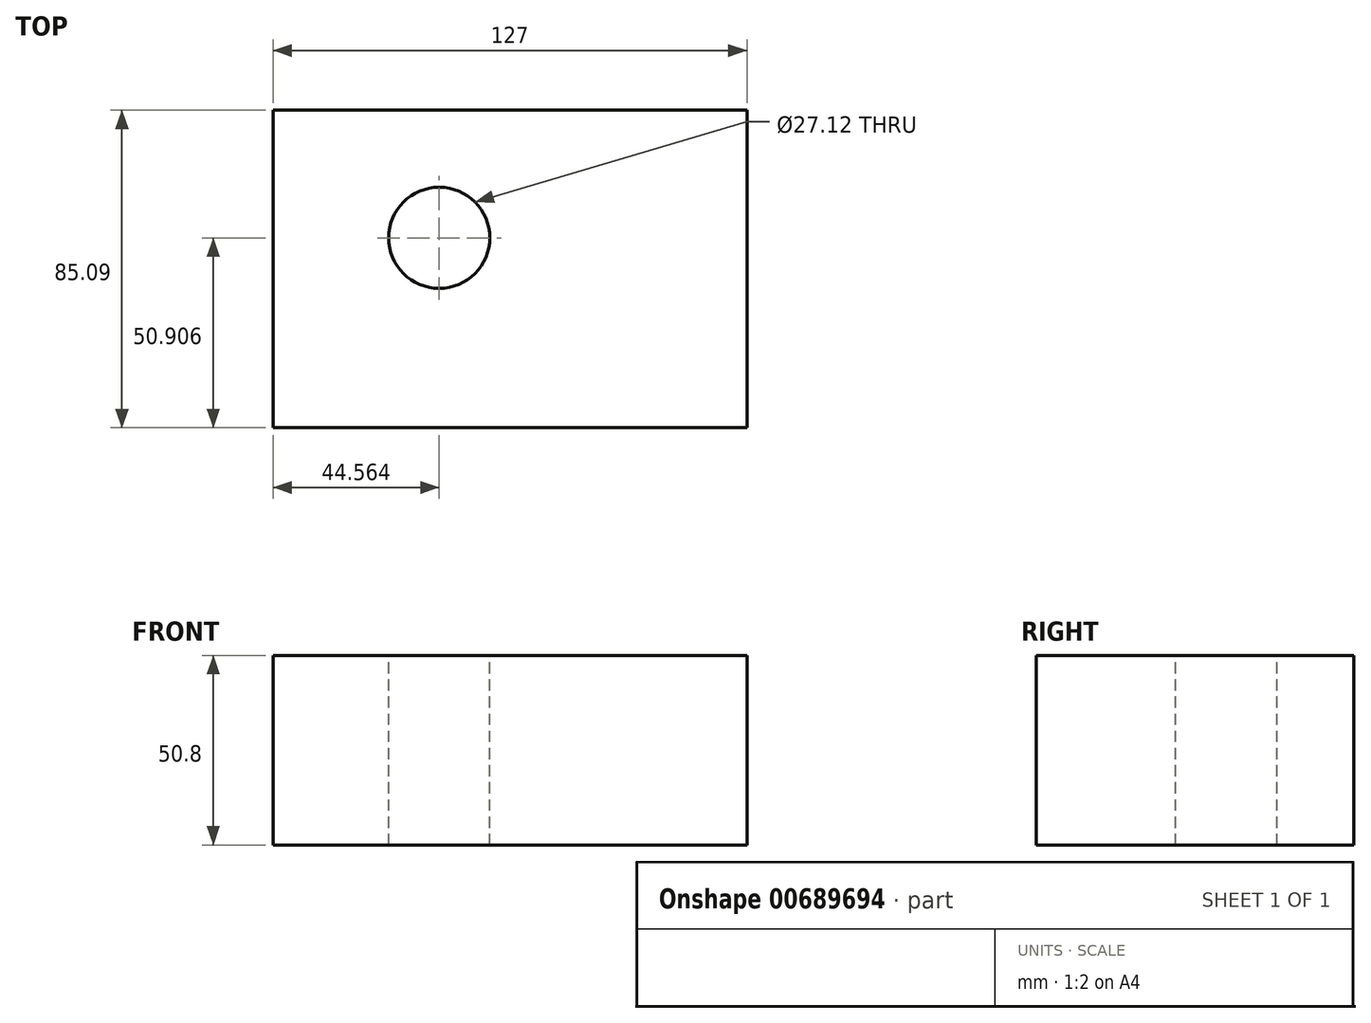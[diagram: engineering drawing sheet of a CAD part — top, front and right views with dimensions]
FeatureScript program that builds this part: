
annotation { "Feature Type Name" : "Feature", "Feature Type Description" : "" }
export const myFeature = defineFeature(function(context is Context, id is Id, definition is map)
    precondition{}
    {
        {
            var Q0;
            Q0=qCreatedBy(makeId("Front.planeOp"),FACE);
            var sketch = newSketch(context, id + "F0", { "sketchPlane" : qUnion([Q0])});
            skLineSegment(sketch, "E0.bottom", {"start": v(-99.64, 38.38) * mm, "end": v(27.36, 38.38) * mm});
            skLineSegment(sketch, "E0.top", {"start": v(-99.64, -12.42) * mm, "end": v(27.36, -12.42) * mm});
            skLineSegment(sketch, "E0.left", {"start": v(-99.64, 38.38) * mm, "end": v(-99.64, -12.42) * mm});
            skLineSegment(sketch, "E0.right", {"start": v(27.36, 38.38) * mm, "end": v(27.36, -12.42) * mm});
            skSolve(sketch);
        }
        {
            var Q0;
            Q0 = qSketchRegion(id + "F0", true);
            extrude(context, id + "F1", {"entities" : qUnion([Q0]), "depth" : 85.1 * mm, "offsetDistance" : 25.4 * mm});
        }
        {
            var Q0;
            Q0=makeQuery(id+"F1.opExtrude","SWEPT_FACE",FACE,{"disambiguationData":[OSD([sQuery(id+"F0.wireOp",EDGE,"E0.bottom")])]});
            var sketch = newSketch(context, id + "F2", { "sketchPlane" : qUnion([Q0])});
            skSolve(sketch);
        }
        {
            var Q0;
            {var subQ0=sQuery(id+"F0.wireOp",EDGE,"E0.bottom");Q0=makeQuery(id+"F2.imprint","IMPRINT",FACE,{"disambiguationData":[TD([[makeQuery(id+"F2.imprint","IMPRINT",EDGE,{"derivedFrom":makeQuery(id+"F1.opExtrude","CAP_EDGE",EDGE,{"disambiguationData":[OSD([subQ0])],"isStart":true})}),-1.0]])]});}
            var sketch = newSketch(context, id + "F3", { "sketchPlane" : qUnion([Q0])});
            skCircle(sketch, "E1", {"center": v(-55.08, -34.18) * mm, "radius": 13.56 * mm});
            skSolve(sketch);
        }
        {
            var Q0;
            Q0=makeQuery(id+"F3.imprint","IMPRINT",FACE,{"disambiguationData":[TD([[makeQuery(id+"F3.imprint","IMPRINT",EDGE,{"derivedFrom":sQuery(id+"F3.wireOp",EDGE,"E1")}),1.0]])]});
            extrude(context, id + "F4", {"entities" : qUnion([Q0]), "operationType" : NewBodyOperationType.REMOVE, "oppositeDirection" : true, "depth" : 73.9 * mm, "offsetDistance" : 25.4 * mm});
        }
    });
